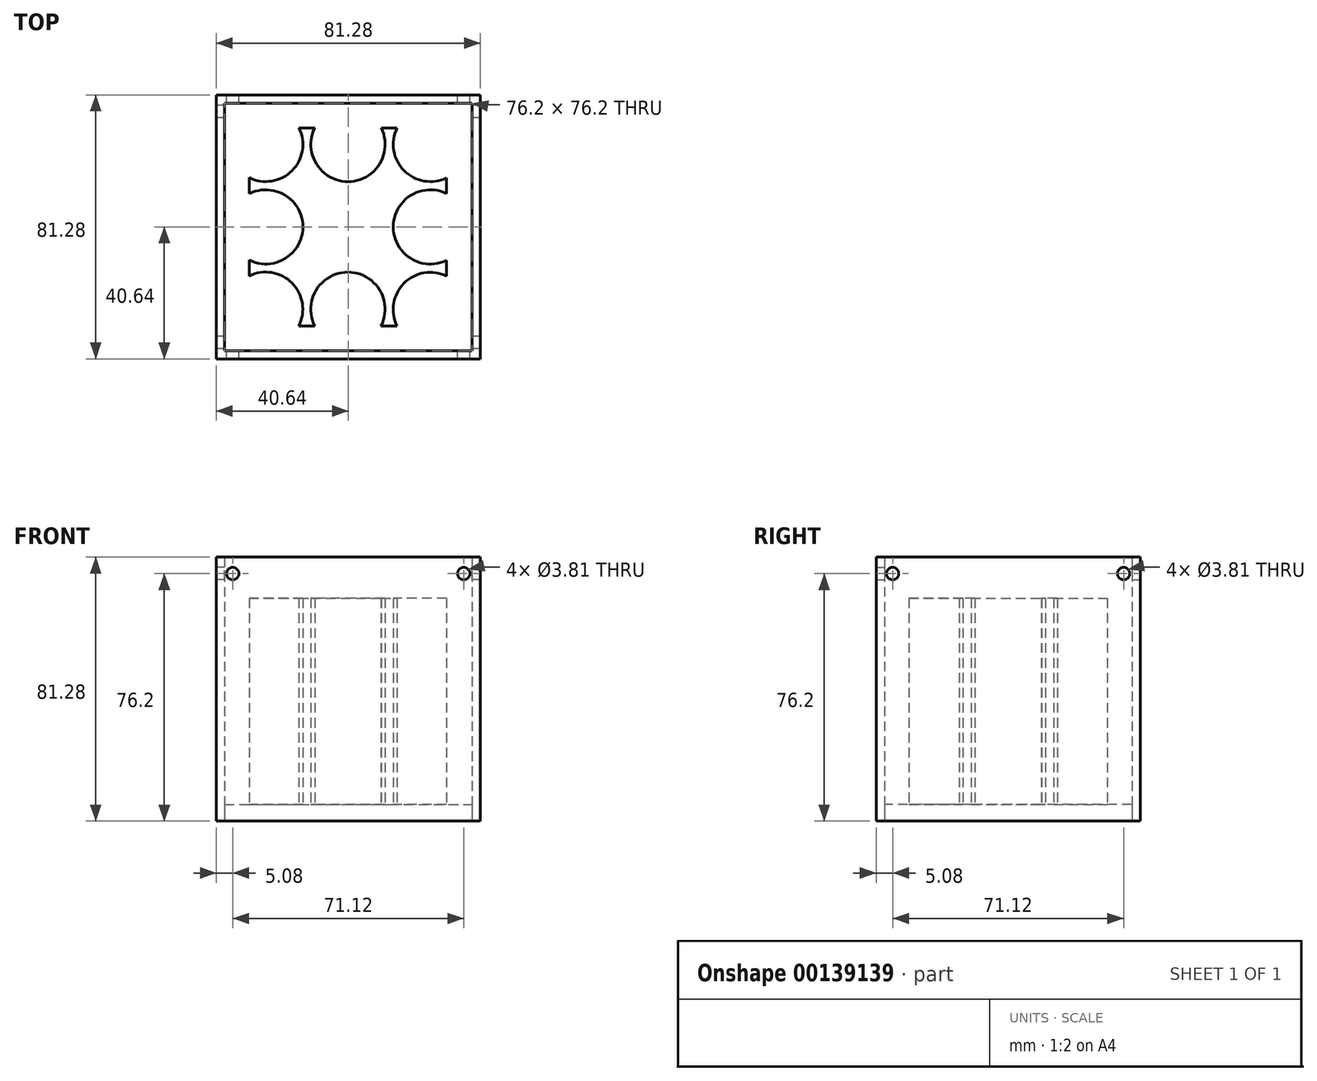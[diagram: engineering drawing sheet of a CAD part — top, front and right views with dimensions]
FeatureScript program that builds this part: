
annotation { "Feature Type Name" : "Feature", "Feature Type Description" : "" }
export const myFeature = defineFeature(function(context is Context, id is Id, definition is map)
    precondition{}
    {
        {
            var Q0;
            Q0=qCreatedBy(makeId("Top.planeOp"),FACE);
            var sketch = newSketch(context, id + "F0", { "sketchPlane" : qUnion([Q0])});
            skLineSegment(sketch, "E0.bottom", {"start": v(0, 0) * mm, "end": v(76.2, 0) * mm});
            skLineSegment(sketch, "E0.top", {"start": v(0, -76.2) * mm, "end": v(76.2, -76.2) * mm});
            skLineSegment(sketch, "E0.left", {"start": v(0, 0) * mm, "end": v(0, -76.2) * mm});
            skLineSegment(sketch, "E0.right", {"start": v(76.2, 0) * mm, "end": v(76.2, -76.2) * mm});
            skLineSegment(sketch, "E1", {"start": v(0, 0) * mm, "end": v(0, 2.54) * mm});
            skLineSegment(sketch, "E2", {"start": v(0, 2.54) * mm, "end": v(-2.54, 2.54) * mm});
            skLineSegment(sketch, "E3.bottom", {"start": v(-2.54, 2.54) * mm, "end": v(78.74, 2.54) * mm});
            skLineSegment(sketch, "E3.top", {"start": v(-2.54, -78.74) * mm, "end": v(78.74, -78.74) * mm});
            skLineSegment(sketch, "E3.left", {"start": v(-2.54, 2.54) * mm, "end": v(-2.54, -78.74) * mm});
            skLineSegment(sketch, "E3.right", {"start": v(78.74, 2.54) * mm, "end": v(78.74, -78.74) * mm});
            skSolve(sketch);
        }
        {
            var Q0;
            Q0=makeQuery(id+"F0.imprint","IMPRINT",FACE,{"disambiguationData":[TD([[makeQuery(id+"F0.imprint","IMPRINT",EDGE,{"derivedFrom":sQuery(id+"F0.wireOp",EDGE,"E0.bottom")}),1.0]])]});
            extrude(context, id + "F1", {"entities" : qUnion([Q0]), "depth" : 81.28 * mm});
        }
        {
            var Q0;
            Q0=qCreatedBy(makeId("Top.planeOp"),FACE);
            var sketch = newSketch(context, id + "F2", { "sketchPlane" : qUnion([Q0])});
            skLineSegment(sketch, "E4.bottom", {"start": v(0, 0) * mm, "end": v(76.2, 0) * mm});
            skLineSegment(sketch, "E4.top", {"start": v(0, -76.2) * mm, "end": v(76.2, -76.2) * mm});
            skLineSegment(sketch, "E4.left", {"start": v(0, 0) * mm, "end": v(0, -76.2) * mm});
            skLineSegment(sketch, "E4.right", {"start": v(76.2, 0) * mm, "end": v(76.2, -76.2) * mm});
            skSolve(sketch);
        }
        {
            var Q0;
            Q0=makeQuery(id+"F2.imprint","IMPRINT",FACE,{"disambiguationData":[TD([[makeQuery(id+"F2.imprint","IMPRINT",EDGE,{"derivedFrom":sQuery(id+"F2.wireOp",EDGE,"E4.bottom")}),-1.0]])]});
            extrude(context, id + "F3", {"entities" : qUnion([Q0]), "depth" : 5.08 * mm});
        }
        {
            var Q0;
            Q0=makeQuery(id+"F3.opExtrude","CAP_FACE",FACE,{"disambiguationData":[OSD([sQuery(id+"F2.wireOp",EDGE,"E4.bottom"),sQuery(id+"F2.wireOp",EDGE,"E4.top"),sQuery(id+"F2.wireOp",EDGE,"E4.left"),sQuery(id+"F2.wireOp",EDGE,"E4.right")])],"isStart":false});
            var sketch = newSketch(context, id + "F4", { "sketchPlane" : qUnion([Q0])});
            skCircle(sketch, "E5", {"center": v(12.7, -12.7) * mm, "radius": 11.43 * mm});
            skCircle(sketch, "E6.MirrorC", {"center": v(38.02, -12.7) * mm, "radius": 11.43 * mm});
            skPoint(sketch, "E7.endSnap0", {"position": v(38.1, 0) * mm});
            skCircle(sketch, "E8.MirrorC", {"center": v(63.4, -12.7) * mm, "radius": 11.43 * mm});
            skCircle(sketch, "E9.MirrorC", {"center": v(12.7, -38.09) * mm, "radius": 11.43 * mm});
            skCircle(sketch, "E10.MirrorC", {"center": v(63.4, -38.09) * mm, "radius": 11.43 * mm});
            skCircle(sketch, "E11.MirrorC", {"center": v(12.68, -63.42) * mm, "radius": 11.43 * mm});
            skCircle(sketch, "E12.MirrorC", {"center": v(63.38, -63.49) * mm, "radius": 11.43 * mm});
            skCircle(sketch, "E13.MirrorC", {"center": v(38, -63.46) * mm, "radius": 11.43 * mm});
            skLineSegment(sketch, "E14", {"start": v(12.7, -12.7) * mm, "end": v(12.7, -7.62) * mm});
            skLineSegment(sketch, "E15", {"start": v(12.7, -7.62) * mm, "end": v(7.6, -7.62) * mm});
            skLineSegment(sketch, "E16.bottom", {"start": v(7.6, -7.62) * mm, "end": v(68.4, -7.62) * mm});
            skLineSegment(sketch, "E16.top", {"start": v(7.6, -68.59) * mm, "end": v(68.4, -68.59) * mm});
            skLineSegment(sketch, "E16.left", {"start": v(7.6, -7.62) * mm, "end": v(7.6, -68.59) * mm});
            skLineSegment(sketch, "E16.right", {"start": v(68.4, -7.62) * mm, "end": v(68.4, -68.59) * mm});
            skSolve(sketch);
        }
        {
            var Q0;
            Q0=makeQuery(id+"F1.opExtrude","SWEPT_FACE",FACE,{"disambiguationData":[OSD([sQuery(id+"F0.wireOp",EDGE,"E3.left")])]});
            var sketch = newSketch(context, id + "F5", { "sketchPlane" : qUnion([Q0])});
            skLineSegment(sketch, "E17", {"start": v(-2.54, 81.28) * mm, "end": v(2.54, 81.28) * mm});
            skLineSegment(sketch, "E18", {"start": v(2.54, 81.28) * mm, "end": v(2.54, 76.2) * mm});
            skCircle(sketch, "E19", {"center": v(2.54, 76.2) * mm, "radius": 1.9 * mm});
            skSolve(sketch);
        }
        {
            var Q0;
            Q0=makeQuery(id+"F5.imprint","IMPRINT",FACE,{"disambiguationData":[TD([[makeQuery(id+"F5.imprint","IMPRINT",EDGE,{"derivedFrom":sQuery(id+"F5.wireOp",EDGE,"E19")}),1.0]])]});
            extrude(context, id + "F6", {"entities" : qUnion([Q0]), "operationType" : NewBodyOperationType.REMOVE, "endBound" : BoundingType.THROUGH_ALL, "oppositeDirection" : true, "depth" : 25.4 * mm});
        }
        {
            var Q0;
            Q0=makeQuery(id+"F1.opExtrude","SWEPT_FACE",FACE,{"disambiguationData":[OSD([sQuery(id+"F0.wireOp",EDGE,"E3.bottom")])]});
            var sketch = newSketch(context, id + "F7", { "sketchPlane" : qUnion([Q0])});
            skLineSegment(sketch, "E20", {"start": v(2.54, 81.28) * mm, "end": v(-2.54, 81.28) * mm});
            skLineSegment(sketch, "E21", {"start": v(-2.54, 81.28) * mm, "end": v(-2.54, 76.2) * mm});
            skCircle(sketch, "E22", {"center": v(-2.54, 76.2) * mm, "radius": 1.9 * mm});
            skSolve(sketch);
        }
        {
            var Q0;
            Q0=makeQuery(id+"F7.imprint","IMPRINT",FACE,{"disambiguationData":[TD([[makeQuery(id+"F7.imprint","IMPRINT",EDGE,{"derivedFrom":sQuery(id+"F7.wireOp",EDGE,"E22")}),1.0]])]});
            extrude(context, id + "F8", {"entities" : qUnion([Q0]), "operationType" : NewBodyOperationType.REMOVE, "endBound" : BoundingType.THROUGH_ALL, "oppositeDirection" : true, "depth" : 25.4 * mm});
        }
        {
            var Q0;
            Q0=makeQuery(id+"F1.opExtrude","SWEPT_FACE",FACE,{"disambiguationData":[OSD([sQuery(id+"F0.wireOp",EDGE,"E3.bottom")])]});
            var sketch = newSketch(context, id + "F9", { "sketchPlane" : qUnion([Q0])});
            skLineSegment(sketch, "E23", {"start": v(-78.74, 81.28) * mm, "end": v(-73.66, 81.28) * mm});
            skLineSegment(sketch, "E24", {"start": v(-73.66, 81.28) * mm, "end": v(-73.66, 76.2) * mm});
            skCircle(sketch, "E25", {"center": v(-73.66, 76.2) * mm, "radius": 1.9 * mm});
            skSolve(sketch);
        }
        {
            var Q0;
            Q0=makeQuery(id+"F9.imprint","IMPRINT",FACE,{"disambiguationData":[TD([[makeQuery(id+"F9.imprint","IMPRINT",EDGE,{"derivedFrom":sQuery(id+"F9.wireOp",EDGE,"E25")}),1.0]])]});
            extrude(context, id + "F10", {"entities" : qUnion([Q0]), "operationType" : NewBodyOperationType.REMOVE, "endBound" : BoundingType.THROUGH_ALL, "oppositeDirection" : true, "depth" : 25.4 * mm});
        }
        {
            var Q0;
            Q0=makeQuery(id+"F1.opExtrude","SWEPT_FACE",FACE,{"disambiguationData":[OSD([sQuery(id+"F0.wireOp",EDGE,"E3.left")])]});
            var sketch = newSketch(context, id + "F11", { "sketchPlane" : qUnion([Q0])});
            skLineSegment(sketch, "E26", {"start": v(78.74, 81.28) * mm, "end": v(73.66, 81.28) * mm});
            skLineSegment(sketch, "E27", {"start": v(73.66, 81.28) * mm, "end": v(73.66, 76.2) * mm});
            skCircle(sketch, "E28", {"center": v(73.66, 76.2) * mm, "radius": 1.9 * mm});
            skSolve(sketch);
        }
        {
            var Q0;
            Q0=makeQuery(id+"F11.imprint","IMPRINT",FACE,{"disambiguationData":[TD([[makeQuery(id+"F11.imprint","IMPRINT",EDGE,{"derivedFrom":sQuery(id+"F11.wireOp",EDGE,"E28")}),1.0]])]});
            extrude(context, id + "F12", {"entities" : qUnion([Q0]), "operationType" : NewBodyOperationType.REMOVE, "endBound" : BoundingType.THROUGH_ALL, "oppositeDirection" : true, "depth" : 25.4 * mm});
        }
        {
            var Q0;
            {var subQ0=sQuery(id+"F4.wireOp",EDGE,"E16.bottom");var subQ9=sQuery(id+"F4.wireOp",EDGE,"E5");var subQ10=makeQuery(id+"F4.imprint","INTERSECT",VERTEX,{"derivedFrom":[subQ9,subQ0]});Q0=makeQuery(id+"F4.imprint","IMPRINT",FACE,{"disambiguationData":[TD([[makeQuery(id+"F4.imprint","IMPRINT",EDGE,{"disambiguationData":[TD([[subQ10,1.0]])],"derivedFrom":subQ9}),-1.0]])]});}
            extrude(context, id + "F13", {"entities" : qUnion([Q0]), "depth" : 63.5 * mm});
        }
    });
